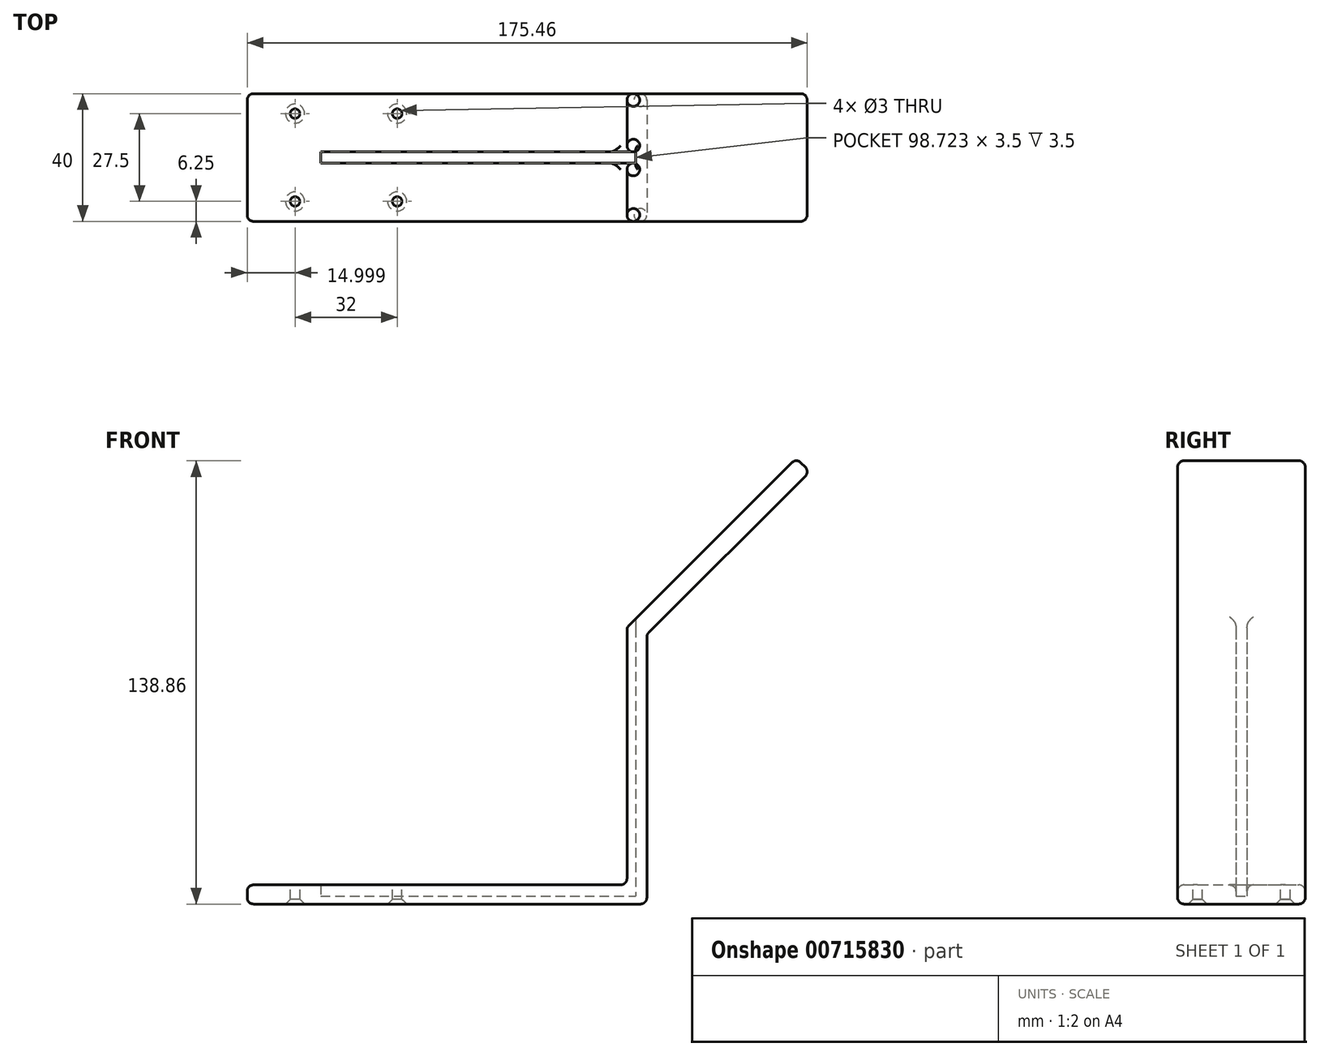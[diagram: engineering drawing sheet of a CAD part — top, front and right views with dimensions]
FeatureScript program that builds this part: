
annotation { "Feature Type Name" : "Feature", "Feature Type Description" : "" }
export const myFeature = defineFeature(function(context is Context, id is Id, definition is map)
    precondition{}
    {
        {
            var Q0;
            Q0=qCreatedBy(makeId("Front.planeOp"),FACE);
            var sketch = newSketch(context, id + "F0", { "sketchPlane" : qUnion([Q0])});
            skLineSegment(sketch, "E0.top", {"start": v(53.8, 4.61) * mm, "end": v(-65.2, 4.61) * mm});
            skPoint(sketch, "E0.middle", {"position": v(0, 0) * mm});
            skLineSegment(sketch, "E1", {"start": v(53.8, 4.61) * mm, "end": v(53.8, 85.29) * mm});
            skPoint(sketch, "E2", {"position": v(-65.2, -1.39) * mm});
            skPoint(sketch, "E3", {"position": v(60.02, -1.39) * mm});
            skPoint(sketch, "E4", {"position": v(60.02, 83.03) * mm});
            skLineSegment(sketch, "E5", {"start": v(60.02, -1.39) * mm, "end": v(60.02, 83.03) * mm});
            skLineSegment(sketch, "E6", {"start": v(60.02, -1.39) * mm, "end": v(-65.2, -1.39) * mm});
            skLineSegment(sketch, "E7", {"start": v(-65.2, -1.39) * mm, "end": v(-65.2, 4.61) * mm});
            skLineSegment(sketch, "E8", {"start": v(53.8, 85.29) * mm, "end": v(106.85, 138.3) * mm});
            skLineSegment(sketch, "E9", {"start": v(106.85, 138.3) * mm, "end": v(111.1, 134.06) * mm});
            skLineSegment(sketch, "E10", {"start": v(60.02, 83.03) * mm, "end": v(111.1, 134.06) * mm});
            skSolve(sketch);
        }
        {
            var Q0;
            Q0=makeQuery(id+"F0.imprint","IMPRINT",FACE,{"disambiguationData":[TD([[makeQuery(id+"F0.imprint","IMPRINT",EDGE,{"derivedFrom":sQuery(id+"F0.wireOp",EDGE,"E0.top")}),1.0]])]});
            extrude(context, id + "F1", {"entities" : qUnion([Q0]), "depth" : 40 * mm, "offsetDistance" : 25 * mm});
        }
        {
            var Q0;
            Q0=makeQuery(id+"F1.opExtrude","SWEPT_FACE",FACE,{"disambiguationData":[OSD([sQuery(id+"F0.wireOp",EDGE,"E6")])]});
            var sketch = newSketch(context, id + "F2", { "sketchPlane" : qUnion([Q0])});
            skPoint(sketch, "E11", {"position": v(60.02, 20) * mm});
            skPoint(sketch, "E12", {"position": v(-65.2, 20) * mm});
            skPoint(sketch, "E13", {"position": v(-42.2, 20) * mm});
            skPoint(sketch, "E14", {"position": v(56.52, 20) * mm});
            skPoint(sketch, "E15", {"position": v(-42.2, 21.75) * mm});
            skLineSegment(sketch, "E16.bottom", {"start": v(-42.2, 21.75) * mm, "end": v(56.52, 21.75) * mm});
            skLineSegment(sketch, "E16.top", {"start": v(-42.2, 18.25) * mm, "end": v(56.52, 18.25) * mm});
            skLineSegment(sketch, "E16.left", {"start": v(-42.2, 21.75) * mm, "end": v(-42.2, 18.25) * mm});
            skLineSegment(sketch, "E16.right", {"start": v(56.52, 21.75) * mm, "end": v(56.52, 18.25) * mm});
            skPoint(sketch, "E17", {"position": v(-50.2, 40) * mm});
            skPoint(sketch, "E18", {"position": v(-50.2, 0) * mm});
            skPoint(sketch, "E19", {"position": v(-18.2, 40) * mm});
            skPoint(sketch, "E20", {"position": v(-18.2, 0) * mm});
            skPoint(sketch, "E21", {"position": v(-65.2, 33.75) * mm});
            skPoint(sketch, "E22", {"position": v(60.02, 33.75) * mm});
            skPoint(sketch, "E23", {"position": v(-65.2, 6.25) * mm});
            skPoint(sketch, "E24", {"position": v(60.02, 6.25) * mm});
            skPoint(sketch, "E25", {"position": v(-50.2, 6.25) * mm});
            skPoint(sketch, "E26", {"position": v(-50.2, 33.75) * mm});
            skPoint(sketch, "E27", {"position": v(-18.2, 33.75) * mm});
            skPoint(sketch, "E28", {"position": v(-18.2, 6.25) * mm});
            skSolve(sketch);
        }
        {
            var Q0;
            Q0=sQuery(id+"F2.wireOp",VERTEX,"E26");
            var Q1;
            Q1=sQuery(id+"F2.wireOp",VERTEX,"E25");
            var Q2;
            Q2=sQuery(id+"F2.wireOp",VERTEX,"E28");
            var Q3;
            Q3=sQuery(id+"F2.wireOp",VERTEX,"E27");
            var Q4;
            Q4=makeQuery(id+"F1.opExtrude","SWEPT_BODY",BODY,{"disambiguationData":[OSD([sQuery(id+"F0.wireOp",EDGE,"E0.top"),sQuery(id+"F0.wireOp",EDGE,"E1"),sQuery(id+"F0.wireOp",EDGE,"E5"),sQuery(id+"F0.wireOp",EDGE,"E6"),sQuery(id+"F0.wireOp",EDGE,"E7"),sQuery(id+"F0.wireOp",EDGE,"E8"),sQuery(id+"F0.wireOp",EDGE,"E9"),sQuery(id+"F0.wireOp",EDGE,"E10")])]});
            hole(context, id + "F3", {"style" : HoleStyle.C_SINK, "endStyle" : HoleEndStyle.BLIND, "holeDiameter" : 3 * mm, "cSinkDiameter" : 6 * mm, "cSinkAngle" : 90 * degree, "majorDiameter" : 5 * mm, "holeDepth" : 40 * mm, "isTappedThrough" : true, "tappedDepth" : 12 * mm, "tapClearance" : 3, "locations" : qUnion([Q0, Q1, Q2, Q3]), "scope" : qUnion([Q4])});
        }
        {
            var Q0;
            Q0=makeQuery(id+"F2.imprint","IMPRINT",FACE,{"disambiguationData":[TD([[makeQuery(id+"F2.imprint","IMPRINT",EDGE,{"derivedFrom":sQuery(id+"F2.wireOp",EDGE,"E16.bottom")}),-1.0]])]});
            extrude(context, id + "F4", {"entities" : qUnion([Q0]), "operationType" : NewBodyOperationType.REMOVE, "oppositeDirection" : true, "depth" : 101 * mm, "offsetDistance" : 25 * mm, "hasSecondDirection" : true, "secondDirectionOppositeDirection" : true, "secondDirectionDepth" : 2.5 * mm});
        }
        {
            var Q0;
            {var subQ2=sQuery(id+"F0.wireOp",EDGE,"E1");Q0=makeQuery(id+"F4.boolean.opBoolean","SPLIT",FACE,{"disambiguationData":[TD([makeQuery(id+"F4.opExtrude","SWEPT_FACE",FACE,{"disambiguationData":[OSD([sQuery(id+"F2.wireOp",EDGE,"E16.bottom")])]})])],"derivedFrom":makeQuery(id+"F1.opExtrude","SWEPT_FACE",FACE,{"disambiguationData":[OSD([subQ2])]})});}
            var Q1;
            {var subQ2=sQuery(id+"F0.wireOp",EDGE,"E1");Q1=makeQuery(id+"F4.boolean.opBoolean","SPLIT",FACE,{"disambiguationData":[TD([makeQuery(id+"F4.opExtrude","SWEPT_FACE",FACE,{"disambiguationData":[OSD([sQuery(id+"F2.wireOp",EDGE,"E16.top")])]})])],"derivedFrom":makeQuery(id+"F1.opExtrude","SWEPT_FACE",FACE,{"disambiguationData":[OSD([subQ2])]})});}
            var Q2;
            Q2=makeQuery(id+"F1.opExtrude","SWEPT_FACE",FACE,{"disambiguationData":[OSD([sQuery(id+"F0.wireOp",EDGE,"E7")])]});
            var Q3;
            Q3=makeQuery(id+"F1.opExtrude","CAP_FACE",FACE,{"disambiguationData":[OSD([sQuery(id+"F0.wireOp",EDGE,"E0.top"),sQuery(id+"F0.wireOp",EDGE,"E1"),sQuery(id+"F0.wireOp",EDGE,"E5"),sQuery(id+"F0.wireOp",EDGE,"E6"),sQuery(id+"F0.wireOp",EDGE,"E7"),sQuery(id+"F0.wireOp",EDGE,"E8"),sQuery(id+"F0.wireOp",EDGE,"E9"),sQuery(id+"F0.wireOp",EDGE,"E10")])],"isStart":true});
            var Q4;
            Q4=makeQuery(id+"F1.opExtrude","CAP_FACE",FACE,{"disambiguationData":[OSD([sQuery(id+"F0.wireOp",EDGE,"E0.top"),sQuery(id+"F0.wireOp",EDGE,"E1"),sQuery(id+"F0.wireOp",EDGE,"E5"),sQuery(id+"F0.wireOp",EDGE,"E6"),sQuery(id+"F0.wireOp",EDGE,"E7"),sQuery(id+"F0.wireOp",EDGE,"E8"),sQuery(id+"F0.wireOp",EDGE,"E9"),sQuery(id+"F0.wireOp",EDGE,"E10")])],"isStart":false});
            var Q5;
            Q5=makeQuery(id+"F1.opExtrude","SWEPT_FACE",FACE,{"disambiguationData":[OSD([sQuery(id+"F0.wireOp",EDGE,"E8")])]});
            var Q6;
            Q6=makeQuery(id+"F1.opExtrude","SWEPT_EDGE",EDGE,{"disambiguationData":[OSD([sQuery(id+"F0.wireOp",EDGE,"E9"),sQuery(id+"F0.wireOp",EDGE,"E10")])]});
            var Q7;
            Q7=makeQuery(id+"F1.opExtrude","SWEPT_EDGE",EDGE,{"disambiguationData":[OSD([sQuery(id+"F0.wireOp",EDGE,"E5"),sQuery(id+"F0.wireOp",EDGE,"E6")])]});
            var Q8;
            Q8=makeQuery(id+"F1.opExtrude","SWEPT_EDGE",EDGE,{"disambiguationData":[OSD([sQuery(id+"F0.wireOp",EDGE,"E5"),sQuery(id+"F0.wireOp",EDGE,"E10")])]});
            fillet(context, id + "F5", {"entities" : qUnion([Q0, Q1, Q2, Q3, Q4, Q5, Q6, Q7, Q8]), "radius" : 2 * mm, "tangentPropagation" : true, "allowEdgeOverflow" : false});
        }
    });
